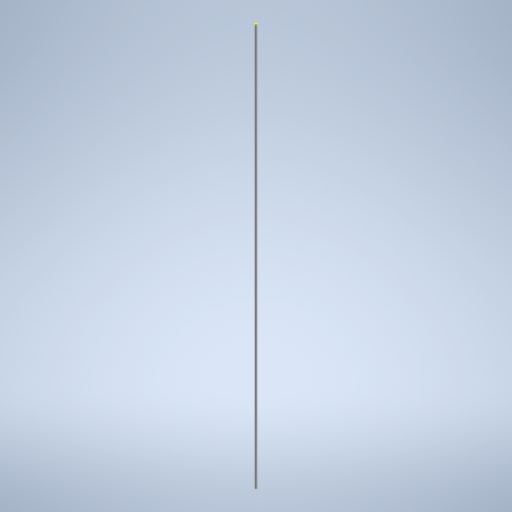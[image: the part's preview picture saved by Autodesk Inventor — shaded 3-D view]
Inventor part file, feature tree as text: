
AUTODESK INVENTOR PART (.ipt)
format: ipt  version: 2023 (Build 270158000, 158)  size: 239,104 bytes
history: native  units: in
note: dims shown in document units (in); Inventor stores cm internally (conversion verified against a paired STEP export)
features: sketch x2, extrude x1, other x1
ambient origin geometry x8: Origin, YZ Plane, XZ Plane, XY Plane, X Axis, Y Axis, Z Axis, Center Point
bodies: Body1 (feature_tree)
feature tree (4):
  extrude  "Extrusion2"  Depth=0.2362in
  sketch  "Esquisse4"
  other  "Filetage1"
  sketch  "Esquisse3"
